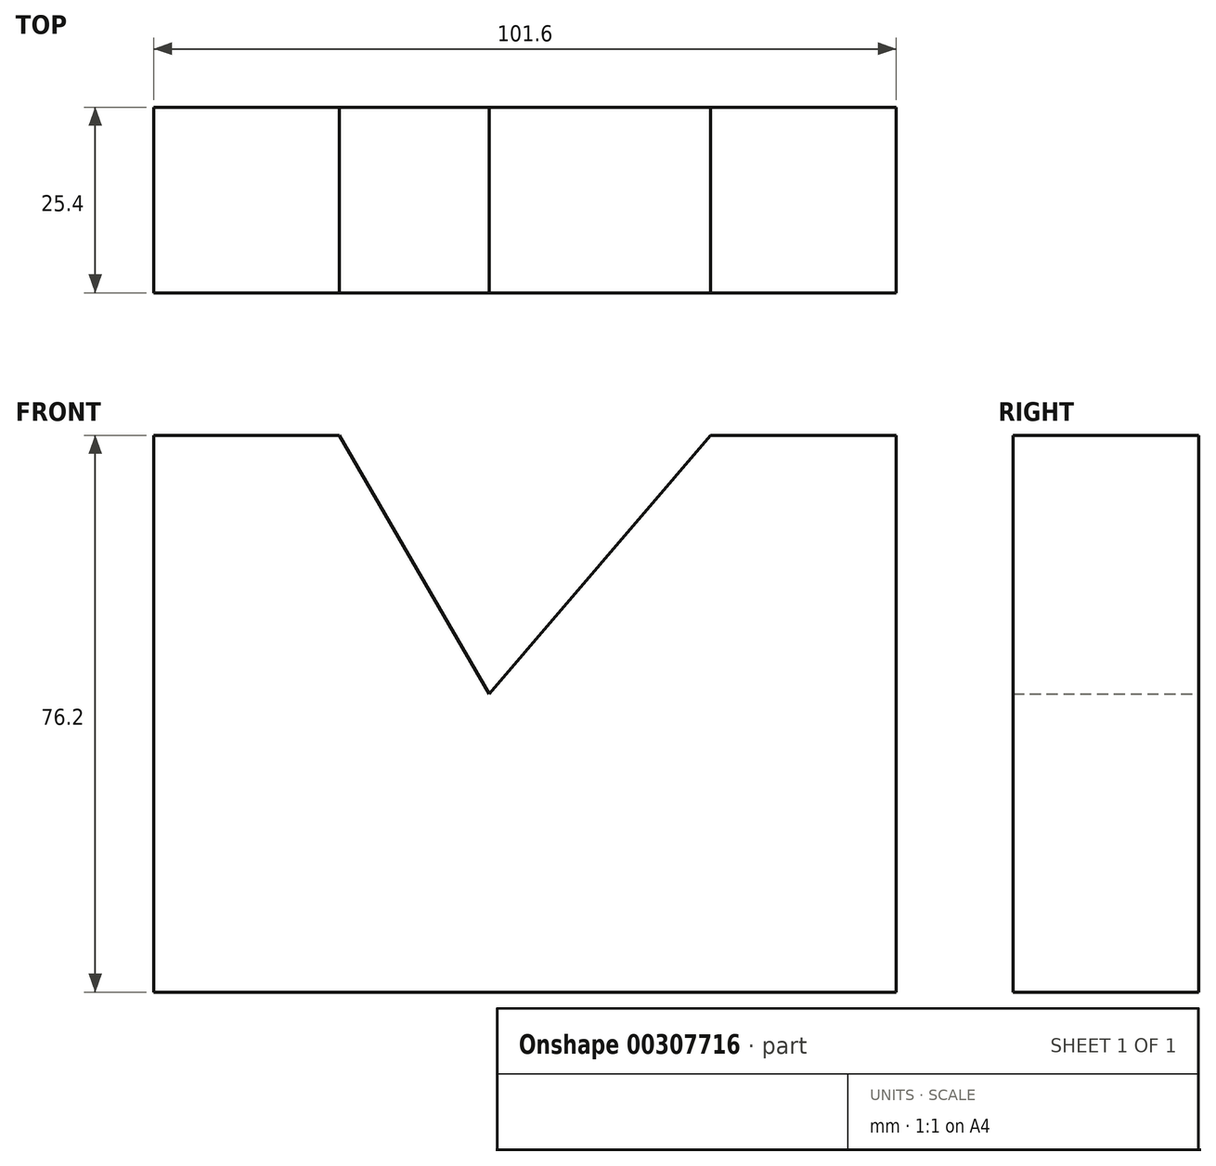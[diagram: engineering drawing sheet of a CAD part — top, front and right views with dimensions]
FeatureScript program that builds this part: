
annotation { "Feature Type Name" : "Feature", "Feature Type Description" : "" }
export const myFeature = defineFeature(function(context is Context, id is Id, definition is map)
    precondition{}
    {
        {
            var Q0;
            Q0=qCreatedBy(makeId("Front.planeOp"),FACE);
            var sketch = newSketch(context, id + "F0", { "sketchPlane" : qUnion([Q0])});
            skLineSegment(sketch, "E0", {"start": v(-34.4, -40.8) * mm, "end": v(67.2, -40.8) * mm});
            skLineSegment(sketch, "E1", {"start": v(67.2, -40.8) * mm, "end": v(67.2, 35.4) * mm});
            skLineSegment(sketch, "E2", {"start": v(67.2, 35.4) * mm, "end": v(41.8, 35.4) * mm});
            skLineSegment(sketch, "E3", {"start": v(-34.4, -40.8) * mm, "end": v(-34.4, 35.4) * mm});
            skLineSegment(sketch, "E4", {"start": v(-34.4, 35.4) * mm, "end": v(-9, 35.4) * mm});
            skLineSegment(sketch, "E5", {"start": v(-9, 35.4) * mm, "end": v(11.5, 0) * mm});
            skLineSegment(sketch, "E6", {"start": v(11.5, 0) * mm, "end": v(41.8, 35.4) * mm});
            skSolve(sketch);
        }
        {
            var Q0;
            Q0=makeQuery(id+"F0.imprint","IMPRINT",FACE,{"disambiguationData":[TD([[makeQuery(id+"F0.imprint","IMPRINT",EDGE,{"derivedFrom":sQuery(id+"F0.wireOp",EDGE,"E0")}),1.0]])]});
            extrude(context, id + "F1", {"entities" : qUnion([Q0]), "depth" : 25.4 * mm});
        }
    });
